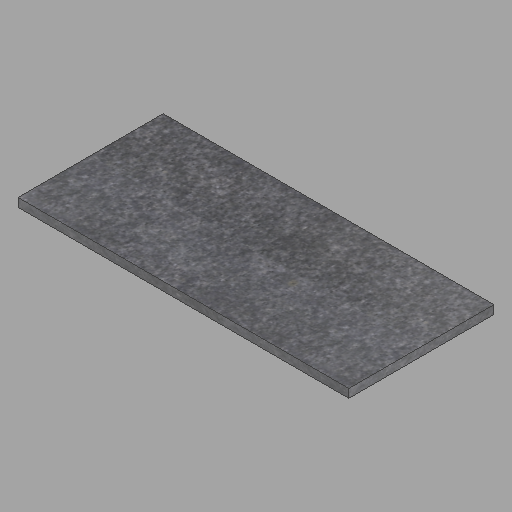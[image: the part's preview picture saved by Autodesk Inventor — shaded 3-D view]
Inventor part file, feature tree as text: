
AUTODESK INVENTOR PART (.ipt)
format: ipt  version: 2023 (Build 270158030, 158C)  size: 208,384 bytes
history: native  units: in
note: dims shown in document units (in); Inventor stores cm internally (conversion verified against a paired STEP export)
features: extrude x1, sketch x1
ambient origin geometry x8: Origin, YZ Plane, XZ Plane, XY Plane, X Axis, Y Axis, Z Axis, Center Point
bodies: Solid1 (feature_tree)
feature tree (2):
  extrude  "Extrusion1"  Depth=34.0in
  sketch  "Sketch1"  dims[d0=77.5in d1=34.0in d2=2.0in d3=0.0in]
